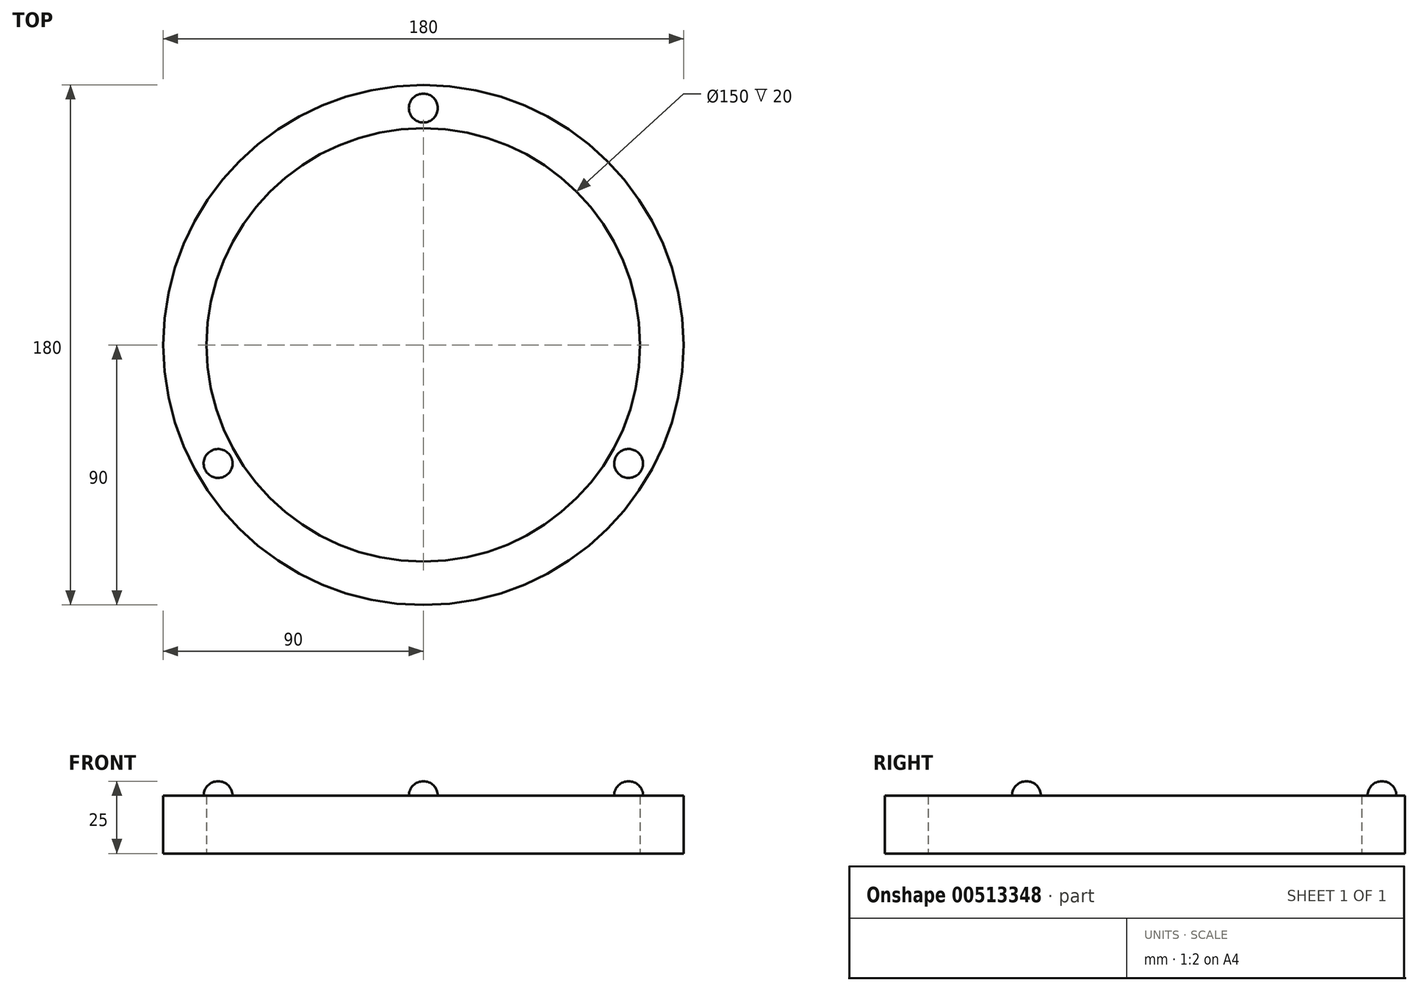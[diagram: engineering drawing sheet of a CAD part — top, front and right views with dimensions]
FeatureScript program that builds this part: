
annotation { "Feature Type Name" : "Feature", "Feature Type Description" : "" }
export const myFeature = defineFeature(function(context is Context, id is Id, definition is map)
    precondition{}
    {
        {
            var Q0;
            Q0=qCreatedBy(makeId("Top.planeOp"),FACE);
            var sketch = newSketch(context, id + "F0", { "sketchPlane" : qUnion([Q0])});
            skCircle(sketch, "E0", {"center": v(0, 0) * mm, "radius": 75 * mm});
            skCircle(sketch, "E1", {"center": v(0, 0) * mm, "radius": 90 * mm});
            skSolve(sketch);
        }
        {
            var Q0;
            Q0 = qSketchRegion(id + "F0", true);
            extrude(context, id + "F1", {"entities" : qUnion([Q0]), "depth" : 20 * mm});
        }
        {
            var Q0;
            Q0=makeQuery(id+"F1.opExtrude","CAP_FACE",FACE,{"disambiguationData":[OSD([sQuery(id+"F0.wireOp",EDGE,"E0"),sQuery(id+"F0.wireOp",EDGE,"E1")])],"isStart":false});
            var sketch = newSketch(context, id + "F2", { "sketchPlane" : qUnion([Q0])});
            skCircle(sketch, "E2.cCircle", {"center": v(0, 0) * mm, "radius": 90 * mm, "construction": true});
            skLineSegment(sketch, "E2.0", {"start": v(155.88, -90) * mm, "end": v(-155.88, -90) * mm});
            skLineSegment(sketch, "E2.1", {"start": v(-155.88, -90) * mm, "end": v(0, 180) * mm});
            skLineSegment(sketch, "E2.2", {"start": v(0, 180) * mm, "end": v(155.88, -90) * mm});
            skPoint(sketch, "E2.0.midPoint", {"position": v(0, -90) * mm});
            skLineSegment(sketch, "E3", {"start": v(155.88, -90) * mm, "end": v(0, 0) * mm, "construction": true});
            skLineSegment(sketch, "E4", {"start": v(-155.88, -90) * mm, "end": v(0, 0) * mm, "construction": true});
            skLineSegment(sketch, "E5", {"start": v(0, 180) * mm, "end": v(0, 0) * mm, "construction": true});
            skArc(sketch, "E6", {"start": v(-66.68, -38.5) * mm, "mid": v(-73.51, -36.67) * mm, "end": v(-75.34, -43.5) * mm});
            skArc(sketch, "E7", {"start": v(75.34, -43.5) * mm, "mid": v(73.51, -36.67) * mm, "end": v(66.68, -38.5) * mm});
            skArc(sketch, "E8", {"start": v(0, 87) * mm, "mid": v(-5, 82) * mm, "end": v(0, 77) * mm});
            skLineSegment(sketch, "E9", {"start": v(-75.34, -43.5) * mm, "end": v(-66.68, -38.5) * mm});
            skLineSegment(sketch, "E10", {"start": v(75.34, -43.5) * mm, "end": v(66.68, -38.5) * mm});
            skLineSegment(sketch, "E11", {"start": v(0, 77) * mm, "end": v(0, 87) * mm});
            skSolve(sketch);
        }
        {
            var Q0;
            Q0=makeQuery(id+"F2.imprint","IMPRINT",FACE,{"disambiguationData":[TD([[makeQuery(id+"F2.imprint","IMPRINT",EDGE,{"derivedFrom":sQuery(id+"F2.wireOp",EDGE,"E6")}),1.0]])]});
            var Q1;
            Q1=sQuery(id+"F2.wireOp",EDGE,"E4");
            revolve(context, id + "F3", {"operationType" : NewBodyOperationType.ADD, "entities" : qUnion([Q0]), "axis" : qUnion([Q1]), "revolveType" : RevolveType.FULL});
        }
        {
            var Q0;
            Q0=makeQuery(id+"F1.opExtrude","CAP_FACE",FACE,{"disambiguationData":[OSD([sQuery(id+"F0.wireOp",EDGE,"E0"),sQuery(id+"F0.wireOp",EDGE,"E1")])],"isStart":false});
            var sketch = newSketch(context, id + "F4", { "sketchPlane" : qUnion([Q0])});
            skCircle(sketch, "E12.cCircle", {"center": v(0, 0) * mm, "radius": 90 * mm, "construction": true});
            skLineSegment(sketch, "E12.0", {"start": v(155.88, -90) * mm, "end": v(-155.88, -90) * mm});
            skLineSegment(sketch, "E12.1", {"start": v(-155.88, -90) * mm, "end": v(0, 180) * mm});
            skLineSegment(sketch, "E12.2", {"start": v(0, 180) * mm, "end": v(155.88, -90) * mm});
            skPoint(sketch, "E12.0.midPoint", {"position": v(0, -90) * mm});
            skLineSegment(sketch, "E13", {"start": v(155.88, -90) * mm, "end": v(0, 0) * mm, "construction": true});
            skLineSegment(sketch, "E14", {"start": v(-155.88, -90) * mm, "end": v(0, 0) * mm, "construction": true});
            skLineSegment(sketch, "E15", {"start": v(0, 180) * mm, "end": v(0, 0) * mm, "construction": true});
            skArc(sketch, "E16", {"start": v(-66.68, -38.5) * mm, "mid": v(-73.51, -36.67) * mm, "end": v(-75.34, -43.5) * mm});
            skArc(sketch, "E17", {"start": v(75.34, -43.5) * mm, "mid": v(73.51, -36.67) * mm, "end": v(66.68, -38.5) * mm});
            skArc(sketch, "E18", {"start": v(0, 87) * mm, "mid": v(-5, 82) * mm, "end": v(0, 77) * mm});
            skLineSegment(sketch, "E19", {"start": v(-75.34, -43.5) * mm, "end": v(-66.68, -38.5) * mm});
            skLineSegment(sketch, "E20", {"start": v(75.34, -43.5) * mm, "end": v(66.68, -38.5) * mm});
            skLineSegment(sketch, "E21", {"start": v(0, 77) * mm, "end": v(0, 87) * mm});
            skSolve(sketch);
        }
        {
            var Q0;
            Q0=makeQuery(id+"F4.imprint","IMPRINT",FACE,{"disambiguationData":[TD([[makeQuery(id+"F4.imprint","IMPRINT",EDGE,{"derivedFrom":sQuery(id+"F4.wireOp",EDGE,"E17")}),1.0]])]});
            var Q1;
            Q1=sQuery(id+"F4.wireOp",EDGE,"E13");
            revolve(context, id + "F5", {"operationType" : NewBodyOperationType.ADD, "entities" : qUnion([Q0]), "axis" : qUnion([Q1]), "revolveType" : RevolveType.FULL});
        }
        {
            var Q0;
            Q0=makeQuery(id+"F1.opExtrude","CAP_FACE",FACE,{"disambiguationData":[OSD([sQuery(id+"F0.wireOp",EDGE,"E0"),sQuery(id+"F0.wireOp",EDGE,"E1")])],"isStart":false});
            var sketch = newSketch(context, id + "F6", { "sketchPlane" : qUnion([Q0])});
            skCircle(sketch, "E22.cCircle", {"center": v(0, 0) * mm, "radius": 90 * mm, "construction": true});
            skLineSegment(sketch, "E22.0", {"start": v(155.88, -90) * mm, "end": v(-155.88, -90) * mm});
            skLineSegment(sketch, "E22.1", {"start": v(-155.88, -90) * mm, "end": v(0, 180) * mm});
            skLineSegment(sketch, "E22.2", {"start": v(0, 180) * mm, "end": v(155.88, -90) * mm});
            skPoint(sketch, "E22.0.midPoint", {"position": v(0, -90) * mm});
            skLineSegment(sketch, "E23", {"start": v(155.88, -90) * mm, "end": v(0, 0) * mm, "construction": true});
            skLineSegment(sketch, "E24", {"start": v(-155.88, -90) * mm, "end": v(0, 0) * mm, "construction": true});
            skLineSegment(sketch, "E25", {"start": v(0, 180) * mm, "end": v(0, 0) * mm, "construction": true});
            skArc(sketch, "E26", {"start": v(-66.68, -38.5) * mm, "mid": v(-73.51, -36.67) * mm, "end": v(-75.34, -43.5) * mm});
            skArc(sketch, "E27", {"start": v(75.34, -43.5) * mm, "mid": v(73.51, -36.67) * mm, "end": v(66.68, -38.5) * mm});
            skArc(sketch, "E28", {"start": v(0, 87) * mm, "mid": v(-5, 82) * mm, "end": v(0, 77) * mm});
            skLineSegment(sketch, "E29", {"start": v(-75.34, -43.5) * mm, "end": v(-66.68, -38.5) * mm});
            skLineSegment(sketch, "E30", {"start": v(75.34, -43.5) * mm, "end": v(66.68, -38.5) * mm});
            skLineSegment(sketch, "E31", {"start": v(0, 77) * mm, "end": v(0, 87) * mm});
            skSolve(sketch);
        }
        {
            var Q0;
            Q0=makeQuery(id+"F6.imprint","IMPRINT",FACE,{"disambiguationData":[TD([[makeQuery(id+"F6.imprint","IMPRINT",EDGE,{"derivedFrom":sQuery(id+"F6.wireOp",EDGE,"E28")}),1.0]])]});
            var Q1;
            Q1=sQuery(id+"F6.wireOp",EDGE,"E25");
            revolve(context, id + "F7", {"operationType" : NewBodyOperationType.ADD, "entities" : qUnion([Q0]), "axis" : qUnion([Q1]), "revolveType" : RevolveType.FULL});
        }
    });
